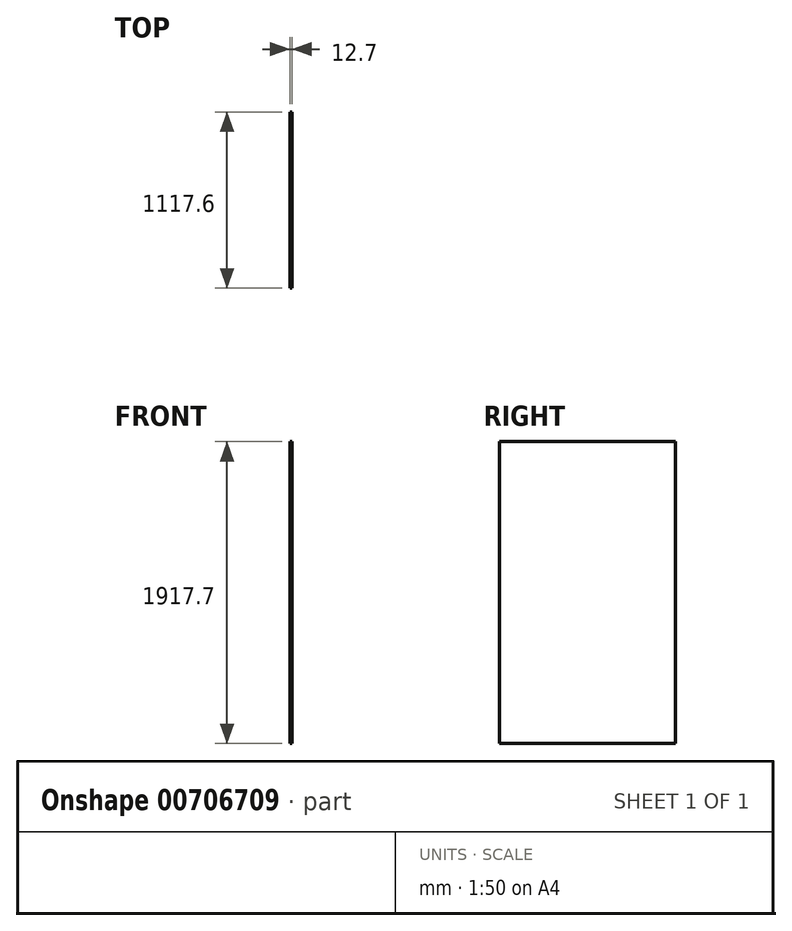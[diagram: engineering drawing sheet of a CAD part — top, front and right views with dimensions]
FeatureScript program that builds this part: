
annotation { "Feature Type Name" : "Feature", "Feature Type Description" : "" }
export const myFeature = defineFeature(function(context is Context, id is Id, definition is map)
    precondition{}
    {
        {
            var Q0;
            Q0=qCreatedBy(makeId("Right.planeOp"),FACE);
            var sketch = newSketch(context, id + "F0", { "sketchPlane" : qUnion([Q0])});
            skLineSegment(sketch, "E0.bottom", {"start": v(0, 0) * mm, "end": v(1117.6, 0) * mm});
            skLineSegment(sketch, "E0.top", {"start": v(0, 1917.7) * mm, "end": v(1117.6, 1917.7) * mm});
            skLineSegment(sketch, "E0.left", {"start": v(0, 0) * mm, "end": v(0, 1917.7) * mm});
            skLineSegment(sketch, "E0.right", {"start": v(1117.6, 0) * mm, "end": v(1117.6, 1917.7) * mm});
            skSolve(sketch);
        }
        {
            var Q0;
            Q0=makeQuery(id+"F0.imprint","IMPRINT",FACE,{"disambiguationData":[TD([[makeQuery(id+"F0.imprint","IMPRINT",EDGE,{"derivedFrom":sQuery(id+"F0.wireOp",EDGE,"E0.bottom")}),1.0]])]});
            extrude(context, id + "F1", {"entities" : qUnion([Q0]), "depth" : 12.7 * mm, "offsetDistance" : 25.4 * mm});
        }
    });
